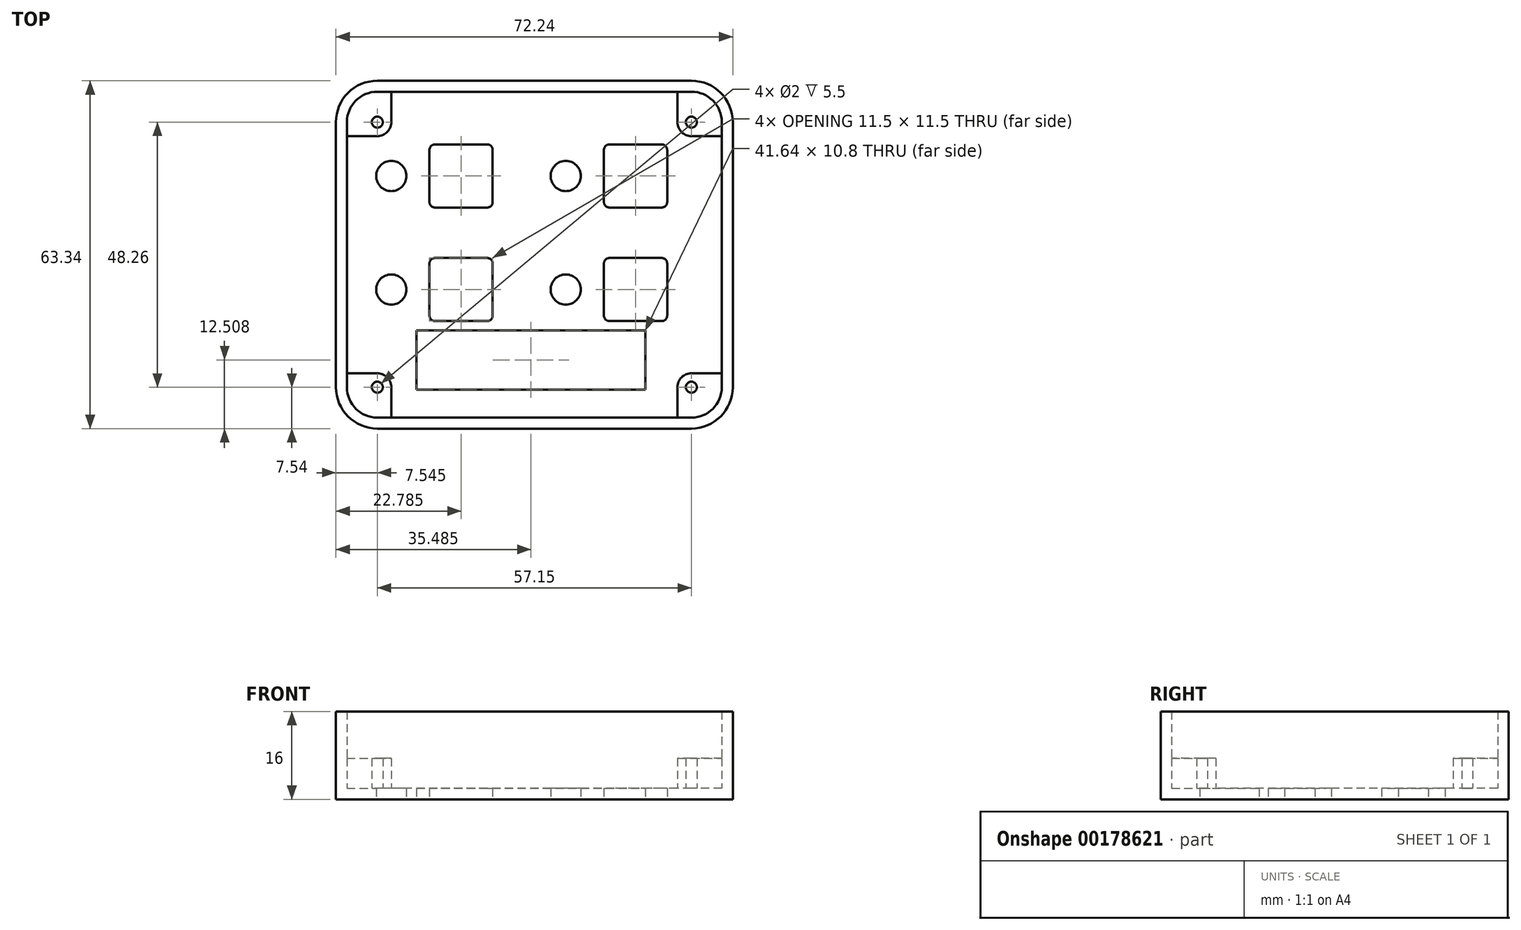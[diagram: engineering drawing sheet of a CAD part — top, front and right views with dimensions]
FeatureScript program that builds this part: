
annotation { "Feature Type Name" : "Feature", "Feature Type Description" : "" }
export const myFeature = defineFeature(function(context is Context, id is Id, definition is map)
    precondition{}
    {
        {
            var Q0;
            Q0=qCreatedBy(makeId("Top.planeOp"),FACE);
            var sketch = newSketch(context, id + "F0", { "sketchPlane" : qUnion([Q0])});
            skLineSegment(sketch, "E0.bottom", {"start": v(28.57, 31.67) * mm, "end": v(-28.58, 31.67) * mm});
            skLineSegment(sketch, "E0.top", {"start": v(28.57, -31.67) * mm, "end": v(-28.58, -31.67) * mm});
            skLineSegment(sketch, "E0.left", {"start": v(36.12, 24.13) * mm, "end": v(36.11, -24.13) * mm});
            skLineSegment(sketch, "E0.right", {"start": v(-36.11, 24.13) * mm, "end": v(-36.12, -24.13) * mm});
            skPoint(sketch, "E0.middle", {"position": v(0, 0) * mm});
            skPoint(sketch, "E1.visualSharp", {"position": v(36.11, -31.67) * mm});
            skArc(sketch, "E1.filletArc", {"start": v(28.57, -31.67) * mm, "mid": v(33.9, -29.46) * mm, "end": v(36.11, -24.13) * mm});
            skPoint(sketch, "E2.visualSharp", {"position": v(-36.12, -31.67) * mm});
            skArc(sketch, "E2.filletArc", {"start": v(-36.12, -24.13) * mm, "mid": v(-33.9, -29.46) * mm, "end": v(-28.58, -31.67) * mm});
            skPoint(sketch, "E3.visualSharp", {"position": v(-36.11, 31.67) * mm});
            skArc(sketch, "E3.filletArc", {"start": v(-28.58, 31.67) * mm, "mid": v(-33.9, 29.46) * mm, "end": v(-36.12, 24.13) * mm});
            skPoint(sketch, "E4.visualSharp", {"position": v(36.12, 31.67) * mm});
            skArc(sketch, "E4.filletArc", {"start": v(36.11, 24.13) * mm, "mid": v(33.9, 29.46) * mm, "end": v(28.57, 31.67) * mm});
            skSolve(sketch);
        }
        {
            var Q0;
            Q0=makeQuery(id+"F0.imprint","IMPRINT",FACE,{"disambiguationData":[TD([[makeQuery(id+"F0.imprint","IMPRINT",EDGE,{"derivedFrom":sQuery(id+"F0.wireOp",EDGE,"E0.bottom")}),1.0]])]});
            extrude(context, id + "F1", {"entities" : qUnion([Q0]), "depth" : 16 * mm});
        }
        {
            var Q0;
            Q0=makeQuery(id+"F1.opExtrude","CAP_FACE",FACE,{"disambiguationData":[OSD([sQuery(id+"F0.wireOp",EDGE,"E0.bottom"),sQuery(id+"F0.wireOp",EDGE,"E0.top"),sQuery(id+"F0.wireOp",EDGE,"E0.left"),sQuery(id+"F0.wireOp",EDGE,"E0.right"),sQuery(id+"F0.wireOp",EDGE,"E1.filletArc"),sQuery(id+"F0.wireOp",EDGE,"E2.filletArc"),sQuery(id+"F0.wireOp",EDGE,"E3.filletArc"),sQuery(id+"F0.wireOp",EDGE,"E4.filletArc")])],"isStart":false});
            shell(context, id + "F2", {"entities" : qUnion([Q0]), "thickness" : 2 * mm});
        }
        {
            var Q0;
            Q0=qCreatedBy(makeId("Top.planeOp"),FACE);
            var sketch = newSketch(context, id + "F3", { "sketchPlane" : qUnion([Q0])});
            skLineSegment(sketch, "E5.bottom", {"start": v(20.19, -13.76) * mm, "end": v(-21.45, -13.76) * mm});
            skLineSegment(sketch, "E5.top", {"start": v(20.19, -24.56) * mm, "end": v(-21.45, -24.56) * mm});
            skLineSegment(sketch, "E5.left", {"start": v(20.19, -13.76) * mm, "end": v(20.19, -24.56) * mm});
            skLineSegment(sketch, "E5.right", {"start": v(-21.45, -13.76) * mm, "end": v(-21.45, -24.56) * mm});
            skPoint(sketch, "E5.middle", {"position": v(-0.63, -19.16) * mm});
            skLineSegment(sketch, "E6.bottom", {"start": v(-18.09, -0.6) * mm, "end": v(-8.59, -0.6) * mm});
            skLineSegment(sketch, "E6.top", {"start": v(-18.09, -12.1) * mm, "end": v(-8.59, -12.1) * mm});
            skLineSegment(sketch, "E6.left", {"start": v(-19.09, -1.6) * mm, "end": v(-19.09, -11.1) * mm});
            skLineSegment(sketch, "E6.right", {"start": v(-7.59, -1.6) * mm, "end": v(-7.59, -11.1) * mm});
            skCircle(sketch, "E7", {"center": v(-26.03, -6.35) * mm, "radius": 2.75 * mm});
            skPoint(sketch, "E7.centerSnap0", {"position": v(-7.59, -6.35) * mm});
            skPoint(sketch, "E8.visualSharp", {"position": v(-19.09, -0.6) * mm});
            skArc(sketch, "E8.filletArc", {"start": v(-18.09, -0.6) * mm, "mid": v(-18.8, -0.9) * mm, "end": v(-19.09, -1.6) * mm});
            skPoint(sketch, "E9.visualSharp", {"position": v(-7.59, -0.6) * mm});
            skArc(sketch, "E9.filletArc", {"start": v(-7.59, -1.6) * mm, "mid": v(-7.88, -0.9) * mm, "end": v(-8.59, -0.6) * mm});
            skPoint(sketch, "E10.visualSharp", {"position": v(-7.59, -12.1) * mm});
            skArc(sketch, "E10.filletArc", {"start": v(-8.59, -12.1) * mm, "mid": v(-7.88, -11.8) * mm, "end": v(-7.59, -11.1) * mm});
            skPoint(sketch, "E11.visualSharp", {"position": v(-19.09, -12.1) * mm});
            skArc(sketch, "E11.filletArc", {"start": v(-19.09, -11.1) * mm, "mid": v(-18.8, -11.8) * mm, "end": v(-18.09, -12.1) * mm});
            skLineSegment(sketch, "E12.0.1.0", {"start": v(-18.09, 20.08) * mm, "end": v(-8.59, 20.08) * mm});
            skLineSegment(sketch, "E12.0.1.1", {"start": v(-7.59, 19.08) * mm, "end": v(-7.59, 9.58) * mm});
            skLineSegment(sketch, "E12.0.1.2", {"start": v(-18.09, 8.58) * mm, "end": v(-8.59, 8.58) * mm});
            skLineSegment(sketch, "E12.0.1.3", {"start": v(-19.09, 19.08) * mm, "end": v(-19.09, 9.58) * mm});
            skCircle(sketch, "E12.0.1.4", {"center": v(-26.03, 14.33) * mm, "radius": 2.75 * mm});
            skArc(sketch, "E12.0.1.5", {"start": v(-18.09, 20.08) * mm, "mid": v(-18.8, 19.79) * mm, "end": v(-19.09, 19.08) * mm});
            skArc(sketch, "E12.0.1.6", {"start": v(-19.09, 9.58) * mm, "mid": v(-18.8, 8.87) * mm, "end": v(-18.09, 8.58) * mm});
            skArc(sketch, "E12.0.1.7", {"start": v(-8.59, 8.58) * mm, "mid": v(-7.88, 8.87) * mm, "end": v(-7.59, 9.58) * mm});
            skArc(sketch, "E12.0.1.8", {"start": v(-7.59, 19.08) * mm, "mid": v(-7.88, 19.79) * mm, "end": v(-8.59, 20.08) * mm});
            skLineSegment(sketch, "E12.1.0.0", {"start": v(13.67, -0.6) * mm, "end": v(23.17, -0.6) * mm});
            skLineSegment(sketch, "E12.1.0.1", {"start": v(24.17, -1.6) * mm, "end": v(24.17, -11.1) * mm});
            skLineSegment(sketch, "E12.1.0.2", {"start": v(13.67, -12.1) * mm, "end": v(23.17, -12.1) * mm});
            skLineSegment(sketch, "E12.1.0.3", {"start": v(12.67, -1.6) * mm, "end": v(12.67, -11.1) * mm});
            skCircle(sketch, "E12.1.0.4", {"center": v(5.72, -6.35) * mm, "radius": 2.75 * mm});
            skArc(sketch, "E12.1.0.5", {"start": v(13.67, -0.6) * mm, "mid": v(12.96, -0.9) * mm, "end": v(12.67, -1.6) * mm});
            skArc(sketch, "E12.1.0.6", {"start": v(12.67, -11.1) * mm, "mid": v(12.96, -11.8) * mm, "end": v(13.67, -12.1) * mm});
            skArc(sketch, "E12.1.0.7", {"start": v(23.17, -12.1) * mm, "mid": v(23.87, -11.8) * mm, "end": v(24.17, -11.1) * mm});
            skArc(sketch, "E12.1.0.8", {"start": v(24.17, -1.6) * mm, "mid": v(23.87, -0.9) * mm, "end": v(23.17, -0.6) * mm});
            skLineSegment(sketch, "E12.1.1.0", {"start": v(13.67, 20.08) * mm, "end": v(23.17, 20.08) * mm});
            skLineSegment(sketch, "E12.1.1.1", {"start": v(24.17, 19.08) * mm, "end": v(24.17, 9.58) * mm});
            skLineSegment(sketch, "E12.1.1.2", {"start": v(13.67, 8.58) * mm, "end": v(23.17, 8.58) * mm});
            skLineSegment(sketch, "E12.1.1.3", {"start": v(12.67, 19.08) * mm, "end": v(12.67, 9.58) * mm});
            skCircle(sketch, "E12.1.1.4", {"center": v(5.72, 14.33) * mm, "radius": 2.75 * mm});
            skArc(sketch, "E12.1.1.5", {"start": v(13.67, 20.08) * mm, "mid": v(12.96, 19.79) * mm, "end": v(12.67, 19.08) * mm});
            skArc(sketch, "E12.1.1.6", {"start": v(12.67, 9.58) * mm, "mid": v(12.96, 8.87) * mm, "end": v(13.67, 8.58) * mm});
            skArc(sketch, "E12.1.1.7", {"start": v(23.17, 8.58) * mm, "mid": v(23.87, 8.87) * mm, "end": v(24.17, 9.58) * mm});
            skArc(sketch, "E12.1.1.8", {"start": v(24.17, 19.08) * mm, "mid": v(23.87, 19.79) * mm, "end": v(23.17, 20.08) * mm});
            skLineSegment(sketch, "E12.direction1", {"start": v(-18.09, -0.6) * mm, "end": v(13.67, -0.6) * mm, "construction": true});
            skLineSegment(sketch, "E12.direction2", {"start": v(-18.09, -0.6) * mm, "end": v(-18.09, 20.08) * mm, "construction": true});
            skSolve(sketch);
        }
        {
            var Q0;
            Q0=qSketchRegion(id+"F3",true);
            extrude(context, id + "F4", {"entities" : qUnion([Q0]), "operationType" : NewBodyOperationType.REMOVE, "endBound" : BoundingType.THROUGH_ALL, "depth" : 25 * mm});
        }
        {
            var Q0;
            Q0=makeQuery(id+"F2.opShell","OFFSET_FACE",FACE,{"disambiguationData":[OSD([sQuery(id+"F0.wireOp",EDGE,"E0.bottom"),sQuery(id+"F0.wireOp",EDGE,"E0.top"),sQuery(id+"F0.wireOp",EDGE,"E0.left"),sQuery(id+"F0.wireOp",EDGE,"E0.right"),sQuery(id+"F0.wireOp",EDGE,"E1.filletArc"),sQuery(id+"F0.wireOp",EDGE,"E2.filletArc"),sQuery(id+"F0.wireOp",EDGE,"E3.filletArc"),sQuery(id+"F0.wireOp",EDGE,"E4.filletArc")])]});
            var sketch = newSketch(context, id + "F5", { "sketchPlane" : qUnion([Q0])});
            skLineSegment(sketch, "E13.top", {"start": v(-34.12, 21.6) * mm, "end": v(-28.57, 21.6) * mm});
            skLineSegment(sketch, "E13.right", {"start": v(-26.03, 29.67) * mm, "end": v(-26.03, 24.13) * mm});
            skPoint(sketch, "E14.visualSharp", {"position": v(-26.03, 21.6) * mm});
            skArc(sketch, "E14.filletArc", {"start": v(-28.57, 21.6) * mm, "mid": v(-26.78, 22.33) * mm, "end": v(-26.03, 24.13) * mm});
            skCircle(sketch, "E15", {"center": v(-28.57, 24.13) * mm, "radius": 1 * mm});
            skLineSegment(sketch, "E16.0", {"start": v(-26.04, 29.67) * mm, "end": v(-28.58, 29.67) * mm});
            skArc(sketch, "E17.0", {"start": v(-28.58, 29.67) * mm, "mid": v(-32.5, 28.05) * mm, "end": v(-34.12, 24.13) * mm});
            skPoint(sketch, "E18.orphan", {"position": v(28.57, 29.67) * mm});
            skLineSegment(sketch, "E19", {"start": v(0, 33.33) * mm, "end": v(0, -33.09) * mm, "construction": true});
            skLineSegment(sketch, "E20", {"start": v(-45.14, 0) * mm, "end": v(38.95, 0) * mm, "construction": true});
            skLineSegment(sketch, "E21", {"start": v(-34.12, 24.13) * mm, "end": v(-34.12, 21.6) * mm});
            skPoint(sketch, "E22.orphan", {"position": v(-36.12, -24.13) * mm});
            skPoint(sketch, "E23.MirrorP", {"position": v(26.03, 21.6) * mm});
            skLineSegment(sketch, "E24.MirrorCS", {"start": v(34.12, 21.6) * mm, "end": v(28.57, 21.6) * mm});
            skLineSegment(sketch, "E25.MirrorCS", {"start": v(26.04, 29.67) * mm, "end": v(28.58, 29.67) * mm});
            skLineSegment(sketch, "E26.MirrorCS", {"start": v(34.12, 24.13) * mm, "end": v(34.12, 21.6) * mm});
            skArc(sketch, "E27.MirrorCS", {"start": v(28.58, 29.67) * mm, "mid": v(32.5, 28.05) * mm, "end": v(34.12, 24.13) * mm});
            skCircle(sketch, "E28.MirrorC", {"center": v(28.57, 24.13) * mm, "radius": 1 * mm});
            skArc(sketch, "E29.MirrorCS", {"start": v(28.57, 21.6) * mm, "mid": v(26.78, 22.33) * mm, "end": v(26.03, 24.13) * mm});
            skLineSegment(sketch, "E30.MirrorCS", {"start": v(26.03, 29.67) * mm, "end": v(26.03, 24.13) * mm});
            skLineSegment(sketch, "E31.MirrorCS", {"start": v(26.04, -29.67) * mm, "end": v(28.58, -29.67) * mm});
            skLineSegment(sketch, "E32.MirrorCS", {"start": v(34.12, -21.6) * mm, "end": v(28.57, -21.6) * mm});
            skArc(sketch, "E33.MirrorCS", {"start": v(28.58, -29.67) * mm, "mid": v(32.5, -28.05) * mm, "end": v(34.12, -24.13) * mm});
            skLineSegment(sketch, "E34.MirrorCS", {"start": v(-34.12, -24.13) * mm, "end": v(-34.12, -21.6) * mm});
            skArc(sketch, "E35.MirrorCS", {"start": v(28.57, -21.6) * mm, "mid": v(26.78, -22.33) * mm, "end": v(26.03, -24.13) * mm});
            skLineSegment(sketch, "E36.MirrorCS", {"start": v(-34.12, -21.6) * mm, "end": v(-28.57, -21.6) * mm});
            skPoint(sketch, "E37.MirrorP", {"position": v(26.03, -21.6) * mm});
            skCircle(sketch, "E38.MirrorC", {"center": v(28.57, -24.13) * mm, "radius": 1 * mm});
            skPoint(sketch, "E39.MirrorP", {"position": v(28.57, -29.67) * mm});
            skLineSegment(sketch, "E40.MirrorCS", {"start": v(-26.04, -29.67) * mm, "end": v(-26.04, -24.13) * mm});
            skLineSegment(sketch, "E41.MirrorCS", {"start": v(26.04, -29.67) * mm, "end": v(26.04, -24.13) * mm});
            skArc(sketch, "E42.MirrorCS", {"start": v(-28.57, -21.6) * mm, "mid": v(-26.78, -22.33) * mm, "end": v(-26.03, -24.13) * mm});
            skLineSegment(sketch, "E43.MirrorCS", {"start": v(34.12, -24.13) * mm, "end": v(34.12, -21.6) * mm});
            skCircle(sketch, "E44.MirrorC", {"center": v(-28.57, -24.13) * mm, "radius": 1 * mm});
            skPoint(sketch, "E45.MirrorP", {"position": v(-26.03, -21.6) * mm});
            skLineSegment(sketch, "E46.MirrorCS", {"start": v(-26.04, -29.67) * mm, "end": v(-28.58, -29.67) * mm});
            skArc(sketch, "E47.MirrorCS", {"start": v(-28.58, -29.67) * mm, "mid": v(-32.5, -28.05) * mm, "end": v(-34.12, -24.13) * mm});
            skSolve(sketch);
        }
        {
            var Q0;
            Q0 = qSketchRegion(id + "F5", true);
            extrude(context, id + "F6", {"entities" : qUnion([Q0]), "operationType" : NewBodyOperationType.ADD, "depth" : 5.5 * mm});
        }
    });
